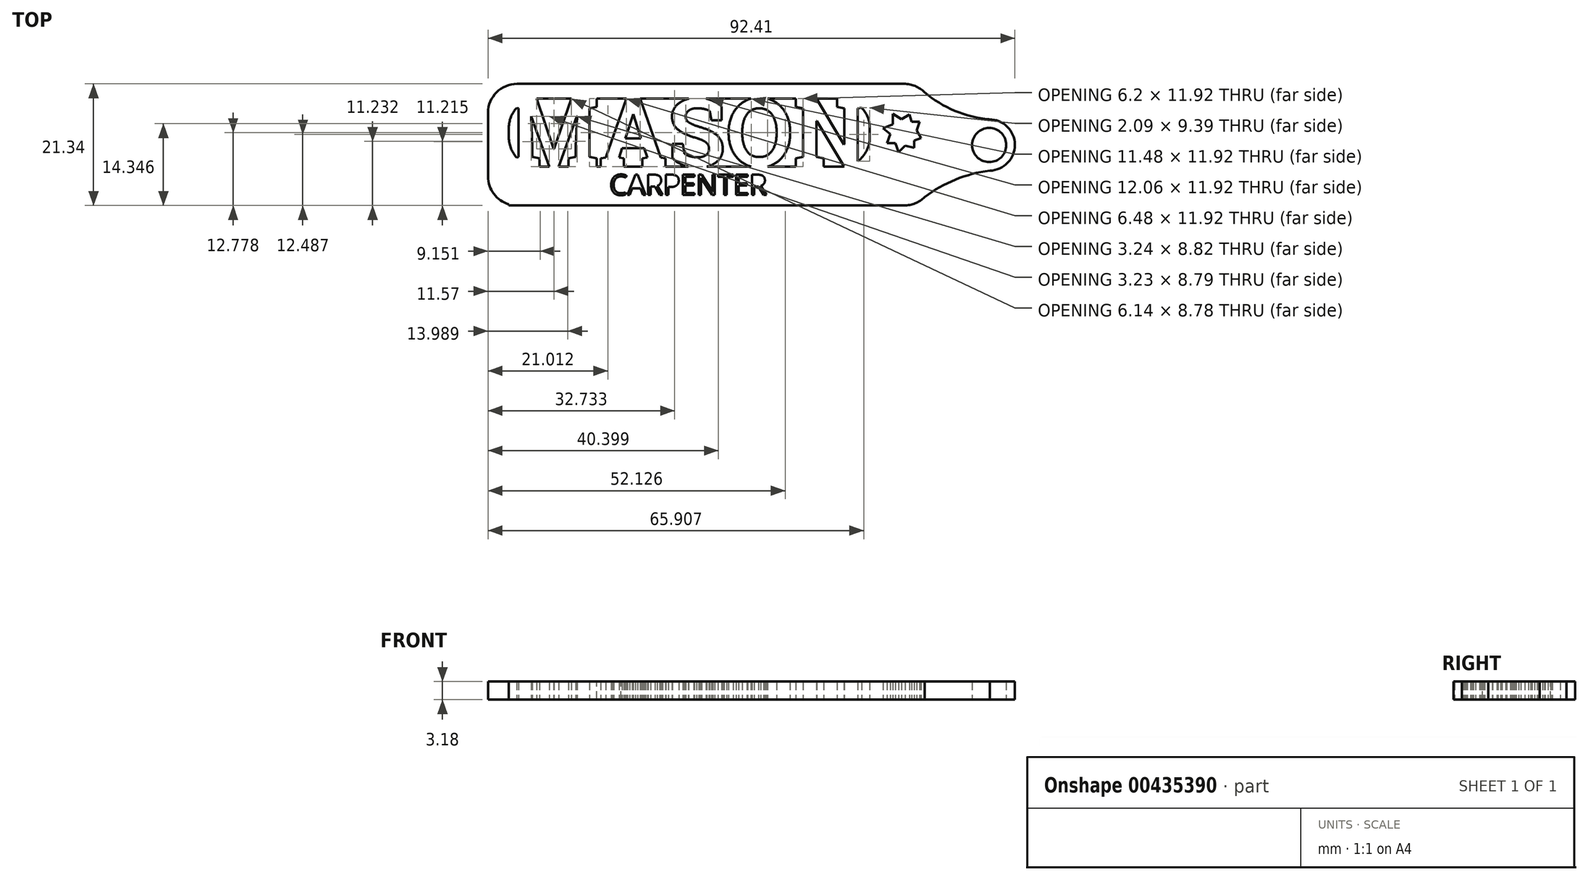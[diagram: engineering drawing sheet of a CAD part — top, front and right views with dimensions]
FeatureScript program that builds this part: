
annotation { "Feature Type Name" : "Feature", "Feature Type Description" : "" }
export const myFeature = defineFeature(function(context is Context, id is Id, definition is map)
    precondition{}
    {
        {
            var Q0;
            Q0=qCreatedBy(makeId("Top.planeOp"),FACE);
            var sketch = newSketch(context, id + "F0", { "sketchPlane" : qUnion([Q0])});
            skText(sketch, "E0", { "text": "MASON\n", "fontName": "RobotoSlab-Bold.ttf"});
            const initialGuessF0  = {"E0": [0, 0, 1, 0, 0.01207]};
            skSetInitialGuess(sketch, initialGuessF0);
            skSolve(sketch);
        }
        {
            var Q0;
            Q0=qCreatedBy(makeId("Top.planeOp"),FACE);
            var sketch = newSketch(context, id + "F1", { "sketchPlane" : qUnion([Q0])});
            skLineSegment(sketch, "E1", {"start": v(5.08, 11.92) * mm, "end": v(58.22, 11.92) * mm});
            skLineSegment(sketch, "E2", {"start": v(63.3, 6.84) * mm, "end": v(63.3, 5.08) * mm});
            skLineSegment(sketch, "E3", {"start": v(58.22, 0) * mm, "end": v(5.08, 0) * mm});
            skLineSegment(sketch, "E4", {"start": v(0, 0) * mm, "end": v(0, -6.82) * mm});
            skLineSegment(sketch, "E5", {"start": v(0, -6.82) * mm, "end": v(69.33, -6.82) * mm});
            skLineSegment(sketch, "E6", {"start": v(74.41, -1.74) * mm, "end": v(74.41, 9.44) * mm});
            skLineSegment(sketch, "E7", {"start": v(69.33, 14.52) * mm, "end": v(1.43, 14.52) * mm});
            skLineSegment(sketch, "E8", {"start": v(-3.65, 9.44) * mm, "end": v(-3.65, -1.74) * mm});
            skLineSegment(sketch, "E9", {"start": v(0, -6.82) * mm, "end": v(1.43, -6.82) * mm});
            skLineSegment(sketch, "E10", {"start": v(0, 5.08) * mm, "end": v(0, 6.84) * mm});
            skPoint(sketch, "E11.visualSharp", {"position": v(-3.65, 14.52) * mm});
            skArc(sketch, "E11.filletArc", {"start": v(1.43, 14.52) * mm, "mid": v(-2.16, 13.03) * mm, "end": v(-3.65, 9.44) * mm});
            skPoint(sketch, "E12.visualSharp", {"position": v(-3.65, -6.82) * mm});
            skArc(sketch, "E12.filletArc", {"start": v(-3.65, -1.74) * mm, "mid": v(-2.16, -5.33) * mm, "end": v(1.43, -6.82) * mm});
            skPoint(sketch, "E13.visualSharp", {"position": v(0, 0) * mm});
            skArc(sketch, "E13.filletArc", {"start": v(0, 5.08) * mm, "mid": v(1.49, 1.49) * mm, "end": v(5.08, 0) * mm});
            skPoint(sketch, "E14.visualSharp", {"position": v(0, 11.92) * mm});
            skArc(sketch, "E14.filletArc", {"start": v(5.08, 11.92) * mm, "mid": v(1.49, 10.43) * mm, "end": v(0, 6.84) * mm});
            skPoint(sketch, "E15.visualSharp", {"position": v(63.3, 11.92) * mm});
            skArc(sketch, "E15.filletArc", {"start": v(63.3, 6.84) * mm, "mid": v(61.81, 10.43) * mm, "end": v(58.22, 11.92) * mm});
            skPoint(sketch, "E16.visualSharp", {"position": v(63.3, 0) * mm});
            skArc(sketch, "E16.filletArc", {"start": v(58.22, 0) * mm, "mid": v(61.81, 1.49) * mm, "end": v(63.3, 5.08) * mm});
            skText(sketch, "E17", { "text": "CARPENTER", "fontName": "OpenSans-Regular.ttf"});
            skPoint(sketch, "E18.visualSharp", {"position": v(74.41, -6.82) * mm});
            skArc(sketch, "E18.filletArc", {"start": v(69.33, -6.82) * mm, "mid": v(72.92, -5.33) * mm, "end": v(74.41, -1.74) * mm});
            skPoint(sketch, "E19.visualSharp", {"position": v(74.41, 14.52) * mm});
            skArc(sketch, "E19.filletArc", {"start": v(74.41, 9.44) * mm, "mid": v(72.92, 13.03) * mm, "end": v(69.33, 14.52) * mm});
            skCircle(sketch, "E20", {"center": v(84.25, 3.8) * mm, "radius": 4.5 * mm});
            skCircle(sketch, "E21", {"center": v(84.25, 3.8) * mm, "radius": 3 * mm});
            skArc(sketch, "E22", {"start": v(84.35, -0.7) * mm, "mid": v(78.34, -2.28) * mm, "end": v(72.92, -5.33) * mm});
            skArc(sketch, "E23", {"start": v(72.92, 13.03) * mm, "mid": v(78.23, 9.8) * mm, "end": v(84.26, 8.3) * mm});
            skCircle(sketch, "E24.cCircle", {"center": v(69.2, 6.02) * mm, "radius": 2.17 * mm, "construction": true});
            skLineSegment(sketch, "E24.0", {"start": v(70.63, 7.88) * mm, "end": v(71.53, 6.33) * mm});
            skLineSegment(sketch, "E24.1", {"start": v(71.53, 6.33) * mm, "end": v(71.07, 4.6) * mm});
            skLineSegment(sketch, "E24.2", {"start": v(71.07, 4.6) * mm, "end": v(69.52, 3.7) * mm});
            skLineSegment(sketch, "E24.3", {"start": v(69.52, 3.7) * mm, "end": v(67.78, 4.15) * mm});
            skLineSegment(sketch, "E24.4", {"start": v(67.78, 4.15) * mm, "end": v(66.88, 5.7) * mm});
            skLineSegment(sketch, "E24.5", {"start": v(66.88, 5.7) * mm, "end": v(67.34, 7.44) * mm});
            skLineSegment(sketch, "E24.6", {"start": v(67.34, 7.44) * mm, "end": v(68.9, 8.35) * mm});
            skLineSegment(sketch, "E24.7", {"start": v(68.9, 8.35) * mm, "end": v(70.63, 7.88) * mm});
            skPoint(sketch, "E24.0.midPoint", {"position": v(71.08, 7.1) * mm});
            skLineSegment(sketch, "E25", {"start": v(67.34, 7.44) * mm, "end": v(67.34, 9.25) * mm});
            skLineSegment(sketch, "E26", {"start": v(67.34, 9.25) * mm, "end": v(68.9, 8.35) * mm});
            skLineSegment(sketch, "E27", {"start": v(68.9, 8.35) * mm, "end": v(70.24, 9.13) * mm});
            skLineSegment(sketch, "E28", {"start": v(70.24, 9.13) * mm, "end": v(70.63, 7.88) * mm});
            skLineSegment(sketch, "E29", {"start": v(70.63, 7.88) * mm, "end": v(72.03, 7.88) * mm});
            skLineSegment(sketch, "E30", {"start": v(72.03, 7.88) * mm, "end": v(71.53, 6.33) * mm});
            skLineSegment(sketch, "E31", {"start": v(71.53, 6.33) * mm, "end": v(72.3, 5.02) * mm});
            skLineSegment(sketch, "E32", {"start": v(72.3, 5.02) * mm, "end": v(71.07, 4.6) * mm});
            skLineSegment(sketch, "E33", {"start": v(71.07, 4.6) * mm, "end": v(71.07, 3.3) * mm});
            skLineSegment(sketch, "E34", {"start": v(71.07, 3.3) * mm, "end": v(69.52, 3.7) * mm});
            skLineSegment(sketch, "E35", {"start": v(69.52, 3.7) * mm, "end": v(68.34, 2.53) * mm});
            skLineSegment(sketch, "E36", {"start": v(68.34, 2.53) * mm, "end": v(67.78, 4.15) * mm});
            skLineSegment(sketch, "E37", {"start": v(67.78, 4.15) * mm, "end": v(66.32, 4.15) * mm});
            skLineSegment(sketch, "E38", {"start": v(66.32, 4.15) * mm, "end": v(66.88, 5.7) * mm});
            skLineSegment(sketch, "E39", {"start": v(66.88, 5.7) * mm, "end": v(65.62, 6.74) * mm});
            skLineSegment(sketch, "E40", {"start": v(65.62, 6.74) * mm, "end": v(67.34, 7.44) * mm});
            const initialGuessF1  = {"E17": [0.01764, -0.00498, 1, 0, 0.0036]};
            skSetInitialGuess(sketch, initialGuessF1);
            skSolve(sketch);
        }
        {
            var Q0;
            Q0 = qSketchRegion(id + "F1", true);
            extrude(context, id + "F2", {"entities" : qUnion([Q0]), "depth" : 3.17 * mm});
        }
        {
            var Q0;
            Q0 = qSketchRegion(id + "F0", true);
            extrude(context, id + "F3", {"entities" : qUnion([Q0]), "operationType" : NewBodyOperationType.ADD, "depth" : 3.17 * mm});
        }
    });
